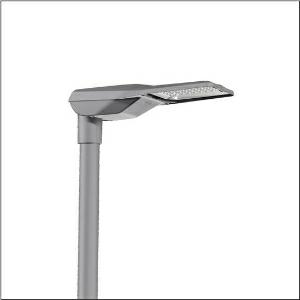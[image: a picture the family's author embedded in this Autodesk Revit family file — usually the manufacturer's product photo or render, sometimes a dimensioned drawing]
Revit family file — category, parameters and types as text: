
# Revit family: streetlight_sl_21_iq_mini___stw1_0a_5xe2e41d08hb_667c
name_source: partatom
category: Lighting Fixtures
units: mm (PartAtom-declared; Revit-internal decimal feet)

## family parameters
Cut with Voids When Loaded = No
Host = Face
Light Source = No
Part Type = Normal
Room Calculation Point = No
Round Connector Dimension = Use Diameter
Shared = No

## types (1)
- --- (1 x LED, 9860 lm, 70.9 W, 4000K)
    Apparent Load = 71 VA
    CIE Flux Codes = 38 75 98 100 100
    Color Rendering = 70
    Color Temperature = 4000K
    Default Elevation = 1800 mm
    Description = Streetlight SL 21 iQ mini, mast luminaire, primary light control with lens, of PMMA, primary optical cover: cover, of toughened safety glass, transparent, light distribution: STW1.0a, light emission: direct distribution, primary light characteristic: asymmetric, installation type: post-top, side-entry, LED, High Power LED, rated luminous flux: 9.860lm, luminous efficacy: 139lm/W, light colour: 740, colour temperature: 4000K, control gear: iQ-Comfort, control: Auto-Match, Temp-Guard, Lumen-Switch, Night-Set, Smart-Wire, Light-Fading, Desk-Remote (wireless, voltage-free reading and setting of iQ features in the workshop via application-optimized NFC function/RFID function), optimised constant luminous flux control (CLO 2.0), pre-setting: linear dimming characteristic, mains connection: 220..240V, AC, 50/60Hz, start of lifetime: 71W, end of service life: 75W, reduction: 31W, luminaire housing, of diecast aluminium, powder-coated, SITECO metallic grey (DB 702S), corrosivity category C5 high according to DIN EN ISO 12944, please order mast flange separately, inclination adjustable: 0°, 5°, 10°, 15°, sealing non-destructively replaceable, multi-level sealing system, length: 628mm, width: 235mm, height: 110mm, mast flange for spigot size: 42mm (side-entry): 5XC10008XM4, 60/48mm (side-entry/post-top): 5XC10108XM2, 76/60mm (side-entry/post-top): 5XC10108XM1, mounting height: 4..8m, protection rating (complete): IP66, insulation class (complete): insulation class II (safety insulation), certification: CE, ENEC, ENEC+, VDE, impact resistance: IK10, permissible operating ambient temperature for outdoor applications: -40..+50°C, standard-compliant lighting for roads and squares, packaging unit: 1 piece

Light Distribution: STW1.0a
    Height = 110 mm
    Lamp = 1 x LED
    Lamp Light Flux = 9860 lm
    Lamp Power = 70.9 W
    Lamp count = 1
    Length = 625 mm
    Luminous efficacy = 139 lm/W
    Manufacturer = Siteco
    ModVariant = No
    Model = 5XE2E41D08HB
    Number of Poles = 1
    OnlyDefault = Yes
    Power Factor = 1
    Product Name = Streetlight SL 21 iQ mini | STW1.0a
    Product group = mast luminaire | pylon top
    ProductGroupID = 6100
    Protection Class = Protection class II
    Protection Degree = IP 66
    RLX_Detail_Level = 1
    RLX_Emergency_Light_Flux = 0 lm
    RLX_Emergency_Type = 0
    RLX_Emergency_Type_DB = No
    RlxData = <blob elided: 26361 chars, md5=bc5e3cba>
    Socket = socket
    Standby Power = 0 W
    System Light Flux = 9860 lm
    System Power = 71 W
    Type Comments = factory setting: luminous flux: 100 % | dim-lin: 254 | 711 mA
    Type Image = l_1003519.jpg
    URL = http://relux.com
    VarID = @adj_157261
    Voltage = 0 V
    Weight = 0.00 kg
    Width = 234 mm

## geometry (parser evidence)
native form markers: Blend x4, Sweep x11
no freeform markers — native parametric forms only
